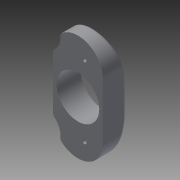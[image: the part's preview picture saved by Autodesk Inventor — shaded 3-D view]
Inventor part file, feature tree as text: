
AUTODESK INVENTOR PART (.ipt)
format: ipt  version: 2015 (Build 190159000, 159)  size: 254,464 bytes
history: native  units: mm
features: extrude x4, sketch x4, fillet x2, chamfer x1
ambient origin geometry x8: Origin, YZ Plane, XZ Plane, XY Plane, X Axis, Y Axis, Z Axis, Center Point
bodies: Solid1 (feature_tree)
feature tree (11):
  extrude  "Extrusion1"  Depth=75.0mm
  extrude  "Extrusion2"  Depth=3.0mm
  extrude  "Extrusion3"  Depth=17.0mm TaperAngle=0.0deg
  fillet  "Fillet1"  Radius=30.0mm
  extrude  "Extrusion4"  Depth=10.0mm
  fillet  "Fillet2"  Radius=35.0mm
  chamfer  "Chamfer1"  Distance=35.0mm
  sketch  "Sketch1"  dims[d0=35.0mm d1=75.0mm]
  sketch  "Sketch2"  dims[d2=30.0mm d7=3.0mm]
  sketch  "Sketch3"  dims[d8=3.0mm d9=17.0mm d10=0.0mm d12=30.0mm]
  sketch  "Sketch4"  dims[d13=10.0mm d14=10.0mm d15=35.0mm d16=0.0mm d17=35.0mm d18=40.0mm d19=17.0mm d20=0.0mm d21=35.0mm d26=12.0mm d27=12.0mm d28=17.0mm d29=0.0mm d30=2.5mm d31=0.7mm d32=2.0mm d33=45.0deg d34=13.0mm d35=13.0mm]
